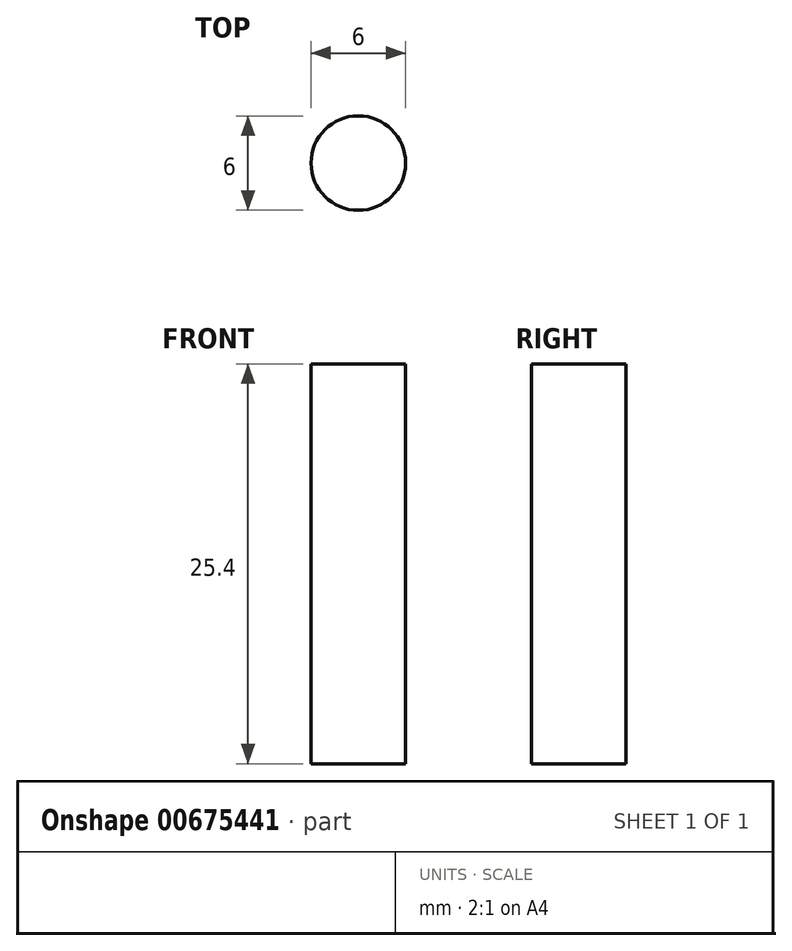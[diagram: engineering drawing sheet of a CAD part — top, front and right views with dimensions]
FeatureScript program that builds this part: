
annotation { "Feature Type Name" : "Feature", "Feature Type Description" : "" }
export const myFeature = defineFeature(function(context is Context, id is Id, definition is map)
    precondition{}
    {
        {
            var Q0;
            Q0=qCreatedBy(makeId("Top.planeOp"),FACE);
            var sketch = newSketch(context, id + "F0", { "sketchPlane" : qUnion([Q0])});
            skLineSegment(sketch, "E0.0", {"start": v(41.93, 3) * mm, "end": v(42.04, 3) * mm});
            skCircle(sketch, "E1", {"center": v(0, 0) * mm, "radius": 3 * mm});
            skSolve(sketch);
        }
        {
            var Q0;
            Q0=makeQuery(id+"F0.imprint","IMPRINT",FACE,{"disambiguationData":[TD([[makeQuery(id+"F0.imprint","IMPRINT",EDGE,{"derivedFrom":sQuery(id+"F0.wireOp",EDGE,"E1")}),1.0]])]});
            extrude(context, id + "F1", {"entities" : qUnion([Q0]), "depth" : 25.4 * mm, "offsetDistance" : 25.4 * mm});
        }
    });
